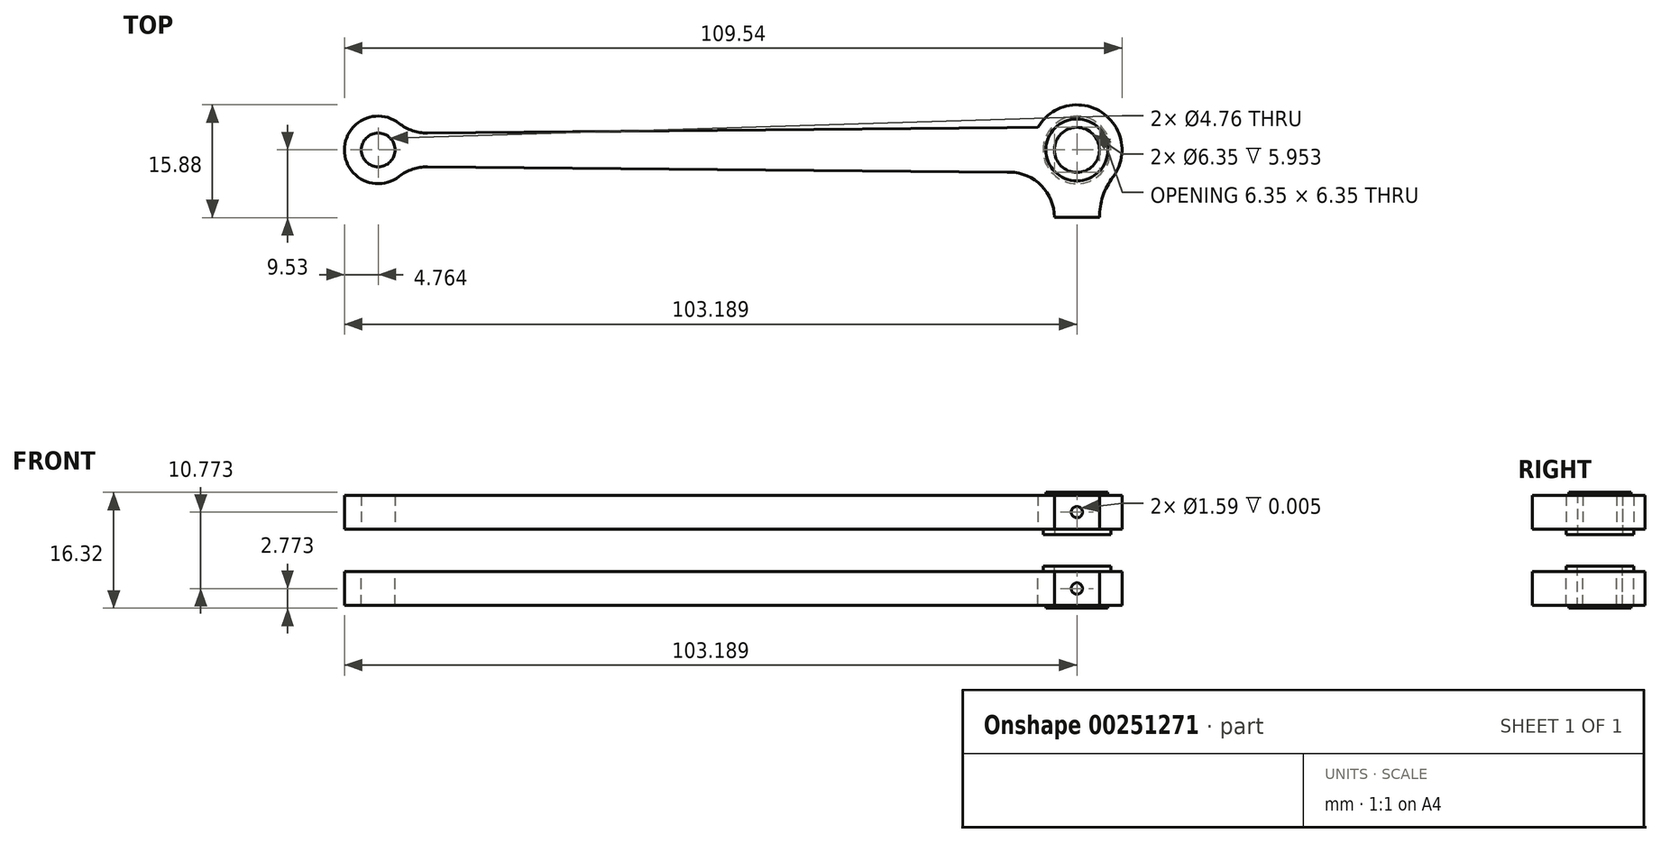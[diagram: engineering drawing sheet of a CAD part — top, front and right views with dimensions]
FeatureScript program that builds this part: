
annotation { "Feature Type Name" : "Feature", "Feature Type Description" : "" }
export const myFeature = defineFeature(function(context is Context, id is Id, definition is map)
    precondition{}
    {
        {
            var Q0;
            Q0=qCreatedBy(makeId("Front.planeOp"),FACE);
            var sketch = newSketch(context, id + "F0", { "sketchPlane" : qUnion([Q0])});
            skLineSegment(sketch, "E0", {"start": v(-31.85, 7.77) * mm, "end": v(77.69, 7.77) * mm});
            skLineSegment(sketch, "E1", {"start": v(77.69, 7.77) * mm, "end": v(77.69, 3) * mm});
            skLineSegment(sketch, "E2", {"start": v(77.69, 3) * mm, "end": v(-31.85, 3) * mm});
            skLineSegment(sketch, "E3", {"start": v(-31.85, 3) * mm, "end": v(-31.85, 7.77) * mm});
            skSolve(sketch);
        }
        {
            var Q0;
            Q0 = qSketchRegion(id + "F0", true);
            extrude(context, id + "F1", {"entities" : qUnion([Q0]), "depth" : 15.88 * mm});
        }
        {
            var Q0;
            Q0=makeQuery(id+"F1.opExtrude","SWEPT_FACE",FACE,{"disambiguationData":[OSD([sQuery(id+"F0.wireOp",EDGE,"E2")])]});
            var sketch = newSketch(context, id + "F2", { "sketchPlane" : qUnion([Q0])});
            skLineSegment(sketch, "E4", {"start": v(-27.09, 15.88) * mm, "end": v(-27.09, 0) * mm});
            skLineSegment(sketch, "E5", {"start": v(-31.85, 6.35) * mm, "end": v(77.69, 6.35) * mm});
            skCircle(sketch, "E6", {"center": v(-27.09, 6.35) * mm, "radius": 4.76 * mm});
            skLineSegment(sketch, "E7", {"start": v(71.34, 15.88) * mm, "end": v(71.34, 0) * mm});
            skCircle(sketch, "E8", {"center": v(71.34, 6.35) * mm, "radius": 6.35 * mm});
            skLineSegment(sketch, "E9", {"start": v(-20.15, 8.73) * mm, "end": v(-20.15, 3.97) * mm});
            skLineSegment(sketch, "E10", {"start": v(61.52, 9.53) * mm, "end": v(61.52, 3.18) * mm});
            skLineSegment(sketch, "E11", {"start": v(-20.15, 3.97) * mm, "end": v(65.84, 3.18) * mm});
            skLineSegment(sketch, "E12", {"start": v(-20.15, 8.73) * mm, "end": v(65.84, 9.52) * mm});
            skArc(sketch, "E13", {"start": v(61.87, 9.49) * mm, "mid": v(66.34, 11.38) * mm, "end": v(68.16, 15.88) * mm});
            skArc(sketch, "E14", {"start": v(74.51, 15.87) * mm, "mid": v(75, 12.86) * mm, "end": v(76.42, 10.16) * mm});
            skArc(sketch, "E15", {"start": v(67.12, 1.6) * mm, "mid": v(65.2, 2.78) * mm, "end": v(62.97, 3.2) * mm});
            skArc(sketch, "E16", {"start": v(-24.14, 10.1) * mm, "mid": v(-22.26, 9.07) * mm, "end": v(-20.15, 8.73) * mm});
            skArc(sketch, "E17", {"start": v(-20.15, 3.97) * mm, "mid": v(-22.26, 3.63) * mm, "end": v(-24.14, 2.6) * mm});
            skSolve(sketch);
        }
        {
            var Q0;
            {var subQ3=sQuery(id+"F2.wireOp",EDGE,"E15");Q0=makeQuery(id+"F2.imprint","IMPRINT",FACE,{"disambiguationData":[TD([[makeQuery(id+"F2.imprint","IMPRINT",EDGE,{"derivedFrom":subQ3}),-1.0]])]});}
            var Q1;
            {var subQ0=sQuery(id+"F2.wireOp",EDGE,"E13");Q1=makeQuery(id+"F2.imprint","IMPRINT",FACE,{"disambiguationData":[TD([[makeQuery(id+"F2.imprint","IMPRINT",EDGE,{"derivedFrom":subQ0}),1.0]])]});}
            var Q2;
            {var subQ10=sQuery(id+"F2.wireOp",EDGE,"E15");Q2=makeQuery(id+"F2.imprint","IMPRINT",FACE,{"disambiguationData":[TD([[makeQuery(id+"F2.imprint","IMPRINT",EDGE,{"derivedFrom":subQ10}),1.0]])]});}
            var Q3;
            {var subQ0=sQuery(id+"F2.wireOp",EDGE,"E4");var subQ1=sQuery(id+"F0.wireOp",EDGE,"E2");var subQ2=makeQuery(id+"F1.opExtrude","CAP_EDGE",EDGE,{"disambiguationData":[OSD([subQ1])],"isStart":false});var subQ3=makeQuery(id+"F2.imprint","INTERSECT",VERTEX,{"derivedFrom":[subQ2,subQ0]});Q3=makeQuery(id+"F2.imprint","IMPRINT",FACE,{"disambiguationData":[TD([[makeQuery(id+"F2.imprint","IMPRINT",EDGE,{"disambiguationData":[TD([[subQ3,-1.0]])],"derivedFrom":subQ0}),-1.0]])]});}
            var Q4;
            {var subQ0=sQuery(id+"F2.wireOp",EDGE,"E4");var subQ1=sQuery(id+"F0.wireOp",EDGE,"E2");var subQ2=makeQuery(id+"F1.opExtrude","CAP_EDGE",EDGE,{"disambiguationData":[OSD([subQ1])],"isStart":true});var subQ3=makeQuery(id+"F2.imprint","INTERSECT",VERTEX,{"derivedFrom":[subQ2,subQ0]});Q4=makeQuery(id+"F2.imprint","IMPRINT",FACE,{"disambiguationData":[TD([[makeQuery(id+"F2.imprint","IMPRINT",EDGE,{"disambiguationData":[TD([[subQ3,1.0]])],"derivedFrom":subQ0}),-1.0]])]});}
            var Q5;
            {var subQ4=sQuery(id+"F2.wireOp",EDGE,"E14");Q5=makeQuery(id+"F2.imprint","IMPRINT",FACE,{"disambiguationData":[TD([[makeQuery(id+"F2.imprint","IMPRINT",EDGE,{"derivedFrom":subQ4}),1.0]])]});}
            var Q6;
            {var subQ1=sQuery(id+"F0.wireOp",EDGE,"E2");var subQ2=makeQuery(id+"F1.opExtrude","SWEPT_EDGE",EDGE,{"disambiguationData":[OSD([sQuery(id+"F0.wireOp",EDGE,"E1"),subQ1])]});var subQ4=makeQuery(id+"F1.opExtrude","CAP_EDGE",EDGE,{"disambiguationData":[OSD([subQ1])],"isStart":true});var subQ6=makeQuery(id+"F2.imprint","INTERSECT",VERTEX,{"derivedFrom":[subQ2,subQ4]});Q6=makeQuery(id+"F2.imprint","IMPRINT",FACE,{"disambiguationData":[TD([[makeQuery(id+"F2.imprint","IMPRINT",EDGE,{"disambiguationData":[TD([[subQ6,-1.0]])],"derivedFrom":subQ4}),-1.0]])]});}
            extrude(context, id + "F3", {"entities" : qUnion([Q0, Q1, Q2, Q3, Q4, Q5, Q6]), "operationType" : NewBodyOperationType.REMOVE, "oppositeDirection" : true, "depth" : 4.76 * mm});
        }
        {
            var Q0;
            Q0=makeQuery(id+"F1.opExtrude","SWEPT_FACE",FACE,{"disambiguationData":[OSD([sQuery(id+"F0.wireOp",EDGE,"E2")])]});
            var sketch = newSketch(context, id + "F4", { "sketchPlane" : qUnion([Q0])});
            skCircle(sketch, "E18", {"center": v(-27.09, 6.35) * mm, "radius": 2.38 * mm});
            skSolve(sketch);
        }
        {
            var Q0;
            Q0 = qSketchRegion(id + "F4", true);
            extrude(context, id + "F5", {"entities" : qUnion([Q0]), "operationType" : NewBodyOperationType.REMOVE, "oppositeDirection" : true, "depth" : 4.76 * mm});
        }
        {
            var Q0;
            Q0=makeQuery(id+"F1.opExtrude","SWEPT_FACE",FACE,{"disambiguationData":[OSD([sQuery(id+"F0.wireOp",EDGE,"E2")])]});
            var sketch = newSketch(context, id + "F6", { "sketchPlane" : qUnion([Q0])});
            skCircle(sketch, "E19", {"center": v(71.34, 6.35) * mm, "radius": 4.76 * mm});
            skSolve(sketch);
        }
        {
            var Q0;
            Q0 = qSketchRegion(id + "F6", true);
            extrude(context, id + "F7", {"entities" : qUnion([Q0]), "operationType" : NewBodyOperationType.ADD, "depth" : 0.8 * mm});
        }
        {
            var Q0;
            Q0=makeQuery(id+"F1.opExtrude","SWEPT_FACE",FACE,{"disambiguationData":[OSD([sQuery(id+"F0.wireOp",EDGE,"E0")])]});
            var sketch = newSketch(context, id + "F8", { "sketchPlane" : qUnion([Q0])});
            skCircle(sketch, "E20", {"center": v(71.34, -6.35) * mm, "radius": 4.37 * mm});
            skSolve(sketch);
        }
        {
            var Q0;
            Q0 = qSketchRegion(id + "F8", true);
            extrude(context, id + "F9", {"entities" : qUnion([Q0]), "operationType" : NewBodyOperationType.ADD, "depth" : 0.4 * mm});
        }
        {
            var Q0;
            Q0=makeQuery(id+"F7.opExtrude","CAP_FACE",FACE,{"disambiguationData":[OSD([sQuery(id+"F6.wireOp",EDGE,"E19")])],"isStart":false});
            var sketch = newSketch(context, id + "F10", { "sketchPlane" : qUnion([Q0])});
            skCircle(sketch, "E21", {"center": v(71.34, 6.35) * mm, "radius": 3.18 * mm});
            skSolve(sketch);
        }
        {
            var Q0;
            Q0 = qSketchRegion(id + "F10", true);
            extrude(context, id + "F11", {"entities" : qUnion([Q0]), "operationType" : NewBodyOperationType.REMOVE, "oppositeDirection" : true, "depth" : 6.35 * mm});
        }
        {
            var Q0;
            Q0=makeQuery(id+"F1.opExtrude","CAP_FACE",FACE,{"disambiguationData":[OSD([sQuery(id+"F0.wireOp",EDGE,"E0"),sQuery(id+"F0.wireOp",EDGE,"E1"),sQuery(id+"F0.wireOp",EDGE,"E2"),sQuery(id+"F0.wireOp",EDGE,"E3")])],"isStart":false});
            var sketch = newSketch(context, id + "F12", { "sketchPlane" : qUnion([Q0])});
            skPoint(sketch, "E22", {"position": v(71.34, 5.39) * mm});
            skCircle(sketch, "E23", {"center": v(71.34, 5.39) * mm, "radius": 0.8 * mm});
            skSolve(sketch);
        }
        {
            var Q0;
            Q0 = qSketchRegion(id + "F12", true);
            extrude(context, id + "F13", {"entities" : qUnion([Q0]), "operationType" : NewBodyOperationType.REMOVE, "oppositeDirection" : true, "depth" : 1 / 203.2 * mm});
        }
        {
            var Q0;
            Q0=qCreatedBy(makeId("Top.planeOp"),FACE);
            var sketch = newSketch(context, id + "F14", { "sketchPlane" : qUnion([Q0])});
            skLineSegment(sketch, "E24.bottom", {"start": v(0, -21.3) * mm, "end": v(57.42, -21.3) * mm});
            skLineSegment(sketch, "E24.top", {"start": v(0, 6.79) * mm, "end": v(57.42, 6.79) * mm});
            skLineSegment(sketch, "E24.left", {"start": v(0, -21.3) * mm, "end": v(0, 6.79) * mm});
            skLineSegment(sketch, "E24.right", {"start": v(57.42, -21.3) * mm, "end": v(57.42, 6.79) * mm});
            skSolve(sketch);
        }
        {
            var Q0;
            Q0=makeQuery(id+"F1.opExtrude","SWEPT_BODY",BODY,{"disambiguationData":[OSD([sQuery(id+"F0.wireOp",EDGE,"E0"),sQuery(id+"F0.wireOp",EDGE,"E1"),sQuery(id+"F0.wireOp",EDGE,"E2"),sQuery(id+"F0.wireOp",EDGE,"E3")])]});
            var Q1;
            Q1=makeQuery(id+"F14.imprint","IMPRINT",FACE,{"disambiguationData":[TD([[makeQuery(id+"F14.imprint","IMPRINT",EDGE,{"derivedFrom":sQuery(id+"F14.wireOp",EDGE,"E24.bottom")}),1.0]])]});
            mirror(context, id + "F15", {"entities" : qUnion([Q0]), "mirrorPlane" : qUnion([Q1])});
        }
    });
